# Revit family: ORBRH
name_source: partatom
category: Mechanical Equipment
units: mm (PartAtom-declared; Revit-internal decimal feet)

## family parameters
Always vertical = Yes
Cut with Voids When Loaded = No
OmniClass Number = 23.40.40.11.17
OmniClass Title = Refrigerated Cases
Part Type = Normal
Room Calculation Point = No
Round Connector Dimension = Use Radius
Shared = No
Work Plane-Based = Yes

## types (3) — shared parameters
27" Shelf = Yes
ANTI CON AMPS = 0 A
BOTTOM ELECTRICAL (default) = Yes
BOTTOM REFRIGERATION (default) = Yes
Certifications = NSF 7, UL471, CSA
DATE = 04/07/2017
DEFROST AMPS = 0 A
DESIGNERS NAME = SHIDDRAMESH
DISCHARGE AIR TEMP = 0 °F
DISCHARGE AIR VELOCITY = - FPM
DRAIN HEATERS AMPS = 0 A
DRAIN LINE CONNECTION = SANITARY LINE CONNECTION
DRAIN LINE DIAMETER = 2"
DRAIN PIPE TYPE = PVC
DRAIN PIPING (default) = Yes
DRIP PAN PLUMB TYPE = HARD
Default Elevation = 48"
Defrost Termination = - °F
Defrost Type = TIMED-OFF DEFROST
Description = Reach-In Rear Load Merchandiser
EQUIPMENT DESCRIPTION = Reach-In Rear Load Merchandiser
EQUIPMENT MARK = ORBRH
GLASS = Glass
HIGH EFFICIENCY FANS AMPS = 0 A
Height = 85 1/4"
Item Description = Reach-In Rear Load Merchandiser
Keynote = ORBRH
LF END = Yes
LIGHT AMPS = 0 A
LIQUID LINE CONNECTION = LIQUID LINE CONNECTION
LIQUID LINE DIAMETER = 0"
LIQUID LINE RADIUS = 0"
LOAD 1 CLASSIFICATION = Lighting
LOAD 1 DESCRIPTION = LIGHT CONNECTION
LOAD 1 PLUG TYPE = HARDWIRED
LOAD 1 POLES = 1
LOAD 1 VOLTAGE = 120 V
LOAD 1 WATTAGE = 0 W
LOAD 2 CLASSIFICATION = Motor
LOAD 2 DESCRIPTION = FAN CONNECTION
LOAD 2 PLUG TYPE = HARDWIRED
LOAD 2 POLES = 1
LOAD 2 VOLTAGE = 120 V
LOAD 2 WATTAGE = 0 W
LOAD 3 CLASSIFICATION = Power
LOAD 3 DESCRIPTION = ANTI-SWEAT CONNECTION
LOAD 3 PLUG TYPE = HARDWIRED
LOAD 3 POLES = 1
LOAD 3 VOLTAGE = 120 V
LOAD 3 WATTAGE = 0 W
LOAD 4 DESCRIPTION = DEFROST HEATER CONNECTION
LOAD 4 PLUG TYPE = HARDWIRED
LOAD 4 POLES = 1
LOAD 4 VOLTAGE = 120 V
LOAD 4 WATTAGE = 0 W
LOAD 5 DESCRIPTION = DRAIN HEATER CONNECTION
LOAD 5 PLUG TYPE = HARDWIRED
LOAD 5 POLES = 1
LOAD 5 VOLTAGE = 120 V
LOAD 5 WATTAGE = 0 W
Legend Number = ORBRH
Manufacturer = HILL PHOENIX
Model = ORBRH
PAINTED METAL UPPER SHELF = PAINTED SHELVES
PRESSURE REGULATOR = 0.00 psi
REFRIGERATION PIPING = COPPER PIPE
RT END = Yes
Refrig Charge Lbs = 0
SANITARY PIPE SIZE = 1"
STAINLESS STEEL = GALVANIZED STEEL
SUCTION LINE CONNECTION = SUCTION LINE CONNECTION
SUCTION LINE DIAMETER = 1"
SUCTION LINE RADIUS = 0"
TOP REFRIGERATION (default) = Yes
URL = http://www.hillphoenix.com
Width = 44"
zero-valued in all types: Defrost Num Day, Evap Temp, Load Mbh, POWER FACTOR

## per-type parameters (varying)
| type | CENTER LINE & DRAIN | Door | Length | NUMBER OF DOORS | number of front doors |
| 8' | 48" | 24 x 64 - 8' & 12' door : 24 x 64 - 12' | 96" | 2 | 2 |
| 12' | 72" | 24 x 64 - 8' & 12' door : 24 x 64 - 12' | 144" | 3 | 3 |
| Sample 1 | 48" | 24 x 64 - 8' & 12' door : 24 x 64 - 8' | 96" | 2 | 3 |

## geometry (parser evidence)
native form markers: Blend x7, Sweep x10
no freeform markers — native parametric forms only
